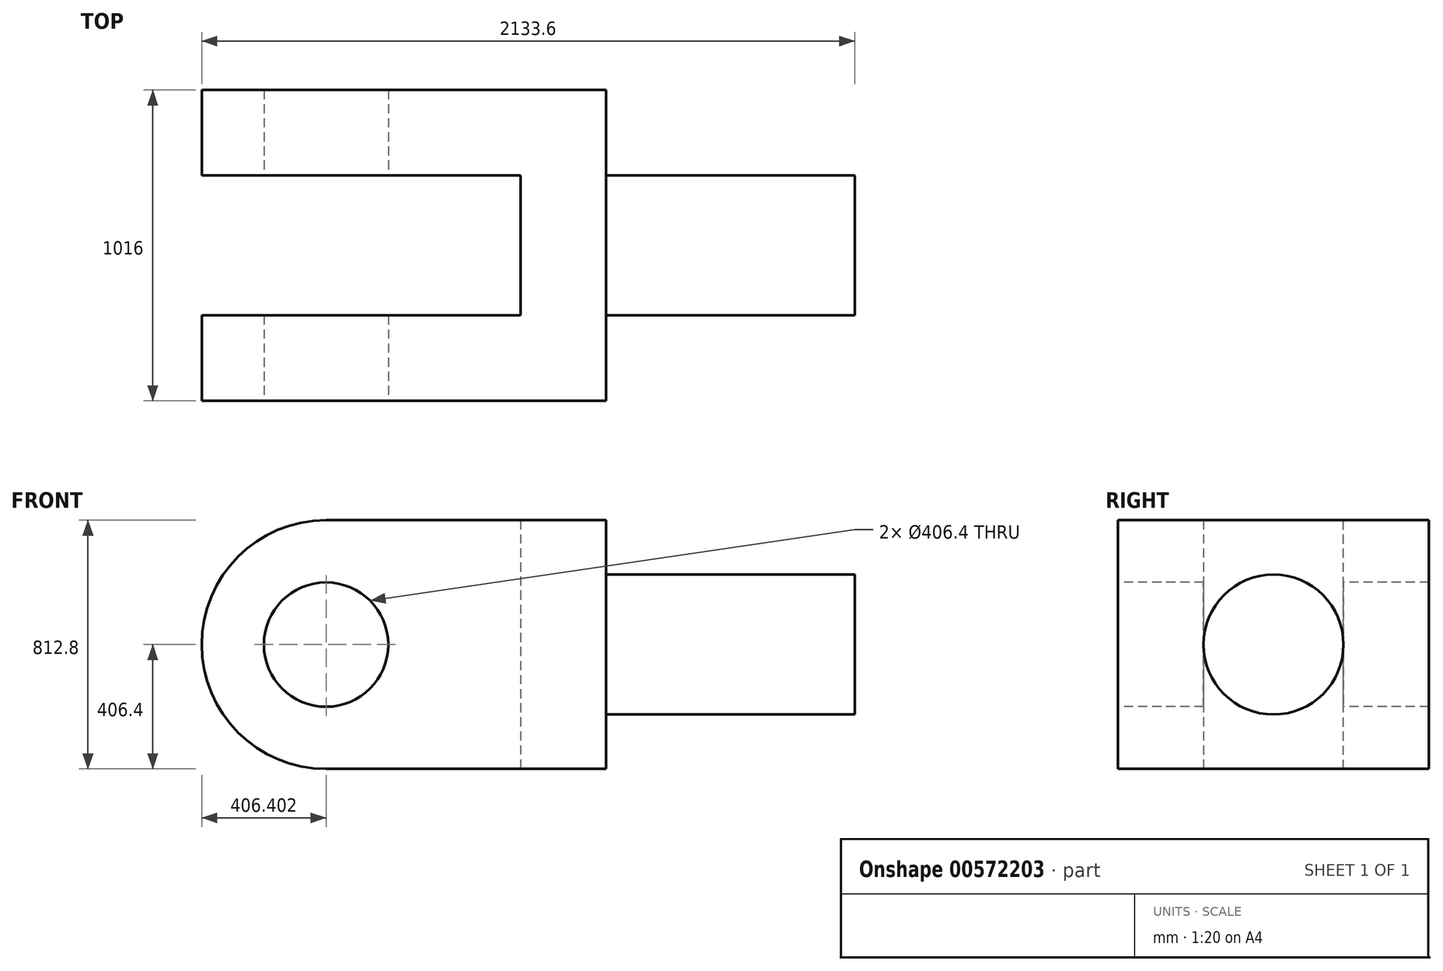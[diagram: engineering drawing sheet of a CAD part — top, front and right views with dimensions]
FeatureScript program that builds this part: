
annotation { "Feature Type Name" : "Feature", "Feature Type Description" : "" }
export const myFeature = defineFeature(function(context is Context, id is Id, definition is map)
    precondition{}
    {
        {
            var Q0;
            Q0=qCreatedBy(makeId("Top.planeOp"),FACE);
            var sketch = newSketch(context, id + "F0", { "sketchPlane" : qUnion([Q0])});
            skLineSegment(sketch, "E0.bottom", {"start": v(419.86, 324.92) * mm, "end": v(1232.66, 324.92) * mm});
            skLineSegment(sketch, "E0.top", {"start": v(419.86, -132.28) * mm, "end": v(1232.66, -132.28) * mm});
            skLineSegment(sketch, "E0.left", {"start": v(419.86, 324.92) * mm, "end": v(419.86, -132.28) * mm});
            skLineSegment(sketch, "E0.right", {"start": v(1232.66, 324.92) * mm, "end": v(1232.66, -132.28) * mm});
            skLineSegment(sketch, "E1", {"start": v(419.86, 324.92) * mm, "end": v(419.86, 604.32) * mm});
            skLineSegment(sketch, "E2", {"start": v(419.86, 604.32) * mm, "end": v(-900.94, 604.32) * mm});
            skLineSegment(sketch, "E3", {"start": v(-900.94, 604.32) * mm, "end": v(-900.94, 324.92) * mm});
            skLineSegment(sketch, "E4", {"start": v(-900.94, 324.92) * mm, "end": v(140.46, 324.92) * mm});
            skLineSegment(sketch, "E5", {"start": v(140.46, 324.92) * mm, "end": v(140.46, -132.28) * mm});
            skLineSegment(sketch, "E6", {"start": v(140.46, -132.28) * mm, "end": v(-900.94, -132.28) * mm});
            skLineSegment(sketch, "E7", {"start": v(-900.94, -132.28) * mm, "end": v(-900.94, -411.68) * mm});
            skLineSegment(sketch, "E8", {"start": v(-900.94, -411.68) * mm, "end": v(419.86, -411.68) * mm});
            skLineSegment(sketch, "E9", {"start": v(419.86, -411.68) * mm, "end": v(419.86, -132.28) * mm});
            skSolve(sketch);
        }
        {
            var Q0;
            Q0=makeQuery(id+"F0.imprint","IMPRINT",FACE,{"disambiguationData":[TD([[makeQuery(id+"F0.imprint","IMPRINT",EDGE,{"derivedFrom":sQuery(id+"F0.wireOp",EDGE,"E0.left")}),-1.0]])]});
            extrude(context, id + "F1", {"entities" : qUnion([Q0]), "depth" : 812.8 * mm, "offsetDistance" : 25.4 * mm});
        }
        {
            var Q0;
            Q0=makeQuery(id+"F1.opExtrude","SWEPT_FACE",FACE,{"disambiguationData":[OSD([sQuery(id+"F0.wireOp",EDGE,"E8")])]});
            var sketch = newSketch(context, id + "F2", { "sketchPlane" : qUnion([Q0])});
            skCircle(sketch, "E10", {"center": v(-494.54, 406.4) * mm, "radius": 203.2 * mm});
            skPoint(sketch, "E10.centerSnap0", {"position": v(-900.94, 406.4) * mm});
            skSolve(sketch);
        }
        {
            var Q0;
            Q0=makeQuery(id+"F2.imprint","IMPRINT",FACE,{"disambiguationData":[TD([[makeQuery(id+"F2.imprint","IMPRINT",EDGE,{"derivedFrom":sQuery(id+"F2.wireOp",EDGE,"E10")}),1.0]])]});
            extrude(context, id + "F3", {"entities" : qUnion([Q0]), "operationType" : NewBodyOperationType.REMOVE, "oppositeDirection" : true, "depth" : 1016 * mm, "offsetDistance" : 25.4 * mm});
        }
        {
            var Q0;
            Q0=makeQuery(id+"F1.opExtrude","SWEPT_FACE",FACE,{"disambiguationData":[OSD([sQuery(id+"F0.wireOp",EDGE,"E0.left"),sQuery(id+"F0.wireOp",EDGE,"E1"),sQuery(id+"F0.wireOp",EDGE,"E9")])]});
            var sketch = newSketch(context, id + "F4", { "sketchPlane" : qUnion([Q0])});
            skCircle(sketch, "E11", {"center": v(96.32, 406.4) * mm, "radius": 228.6 * mm});
            skPoint(sketch, "E11.centerSnap0", {"position": v(96.32, 0) * mm});
            skPoint(sketch, "E11.centerSnap1", {"position": v(604.32, 406.4) * mm});
            skSolve(sketch);
        }
        {
            var Q0;
            Q0 = qSketchRegion(id + "F4", true);
            extrude(context, id + "F5", {"entities" : qUnion([Q0]), "operationType" : NewBodyOperationType.ADD, "depth" : 812.8 * mm, "offsetDistance" : 25.4 * mm});
        }
        {
            var Q0;
            Q0=makeQuery(id+"F1.opExtrude","CAP_EDGE",EDGE,{"disambiguationData":[OSD([sQuery(id+"F0.wireOp",EDGE,"E3")])],"isStart":false});
            var Q1;
            Q1=makeQuery(id+"F1.opExtrude","CAP_EDGE",EDGE,{"disambiguationData":[OSD([sQuery(id+"F0.wireOp",EDGE,"E3")])],"isStart":true});
            fillet(context, id + "F6", {"entities" : qUnion([Q0, Q1]), "radius" : 406.4 * mm, "tangentPropagation" : true, "allowEdgeOverflow" : false});
        }
        {
            var Q0;
            Q0=makeQuery(id+"F1.opExtrude","CAP_EDGE",EDGE,{"disambiguationData":[OSD([sQuery(id+"F0.wireOp",EDGE,"E7")])],"isStart":false});
            var Q1;
            Q1=makeQuery(id+"F1.opExtrude","CAP_EDGE",EDGE,{"disambiguationData":[OSD([sQuery(id+"F0.wireOp",EDGE,"E7")])],"isStart":true});
            fillet(context, id + "F7", {"entities" : qUnion([Q0, Q1]), "radius" : 406.4 * mm, "tangentPropagation" : true, "allowEdgeOverflow" : false});
        }
    });
